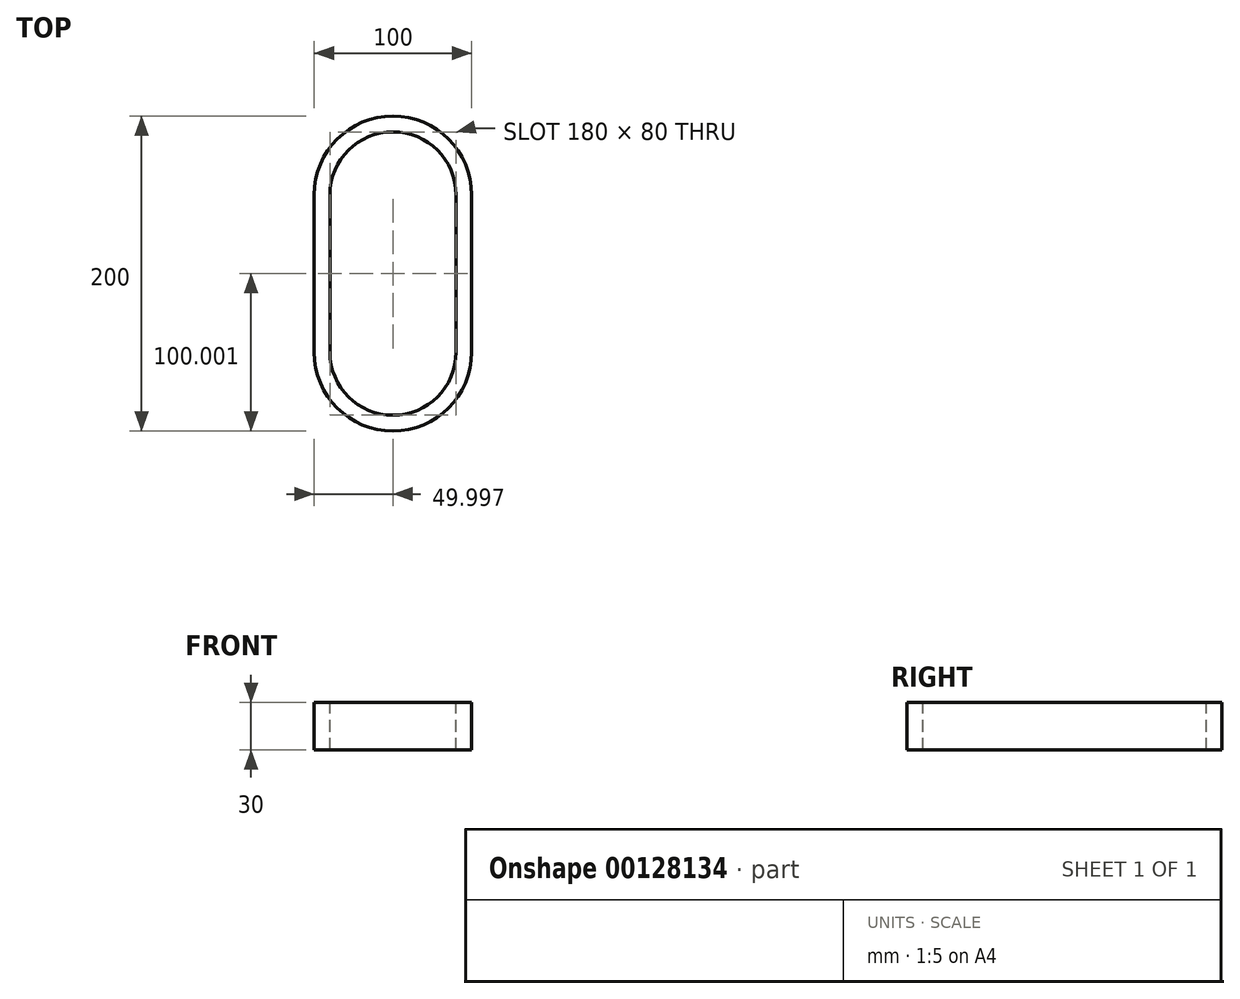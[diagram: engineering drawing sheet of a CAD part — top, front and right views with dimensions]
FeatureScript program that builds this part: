
annotation { "Feature Type Name" : "Feature", "Feature Type Description" : "" }
export const myFeature = defineFeature(function(context is Context, id is Id, definition is map)
    precondition{}
    {
        {
            var Q0;
            Q0=qCreatedBy(makeId("Top.planeOp"),FACE);
            var sketch = newSketch(context, id + "F0", { "sketchPlane" : qUnion([Q0])});
            skArc(sketch, "E0", {"start": v(42.52, 123.17) * mm, "mid": v(-7.48, 173.17) * mm, "end": v(-57.48, 123.17) * mm});
            skArc(sketch, "E1", {"start": v(-57.48, 23.17) * mm, "mid": v(-7.48, -26.83) * mm, "end": v(42.52, 23.17) * mm});
            skLineSegment(sketch, "E2.left", {"start": v(-7.29, 173.17) * mm, "end": v(-7.29, -26.83) * mm, "construction": true});
            skLineSegment(sketch, "E3", {"start": v(42.52, 123.17) * mm, "end": v(42.52, 23.17) * mm});
            skLineSegment(sketch, "E4", {"start": v(-57.48, 123.17) * mm, "end": v(-57.48, 23.17) * mm});
            skSolve(sketch);
        }
        {
            var Q0;
            Q0 = qSketchRegion(id + "F0", true);
            extrude(context, id + "F1", {"entities" : qUnion([Q0]), "oppositeDirection" : true, "depth" : 30 * mm});
        }
        {
            var Q0;
            Q0=makeQuery(id+"F1.opExtrude","CAP_FACE",FACE,{"disambiguationData":[OSD([sQuery(id+"F0.wireOp",EDGE,"E0"),sQuery(id+"F0.wireOp",EDGE,"E1"),sQuery(id+"F0.wireOp",EDGE,"E3"),sQuery(id+"F0.wireOp",EDGE,"E4")])],"isStart":true});
            var sketch = newSketch(context, id + "F2", { "sketchPlane" : qUnion([Q0])});
            skLineSegment(sketch, "E5.0", {"start": v(32.52, 23.17) * mm, "end": v(32.52, 123.17) * mm});
            skArc(sketch, "E5.1", {"start": v(-47.48, 23.17) * mm, "mid": v(-7.48, -16.83) * mm, "end": v(32.52, 23.17) * mm});
            skLineSegment(sketch, "E5.2", {"start": v(-47.48, 123.17) * mm, "end": v(-47.48, 23.17) * mm});
            skArc(sketch, "E5.3", {"start": v(32.52, 123.17) * mm, "mid": v(-7.48, 163.17) * mm, "end": v(-47.48, 123.17) * mm});
            skSolve(sketch);
        }
        {
            var Q0;
            Q0=makeQuery(id+"F2.imprint","IMPRINT",FACE,{"disambiguationData":[TD([[makeQuery(id+"F2.imprint","IMPRINT",EDGE,{"derivedFrom":sQuery(id+"F2.wireOp",EDGE,"E5.0")}),1.0]])]});
            extrude(context, id + "F3", {"entities" : qUnion([Q0]), "operationType" : NewBodyOperationType.REMOVE, "endBound" : BoundingType.THROUGH_ALL, "oppositeDirection" : true, "depth" : 25 * mm});
        }
    });
